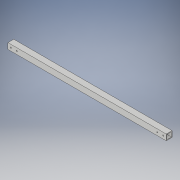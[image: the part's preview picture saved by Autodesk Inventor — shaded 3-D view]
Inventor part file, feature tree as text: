
AUTODESK INVENTOR PART (.ipt)
format: ipt  version: 2018 (Build 220112000, 112)  size: 121,856 bytes
history: native  units: in
note: dims shown in document units (in); Inventor stores cm internally (conversion verified against a paired STEP export)
features: extrude x2, sketch x2
ambient origin geometry x8: Origin, YZ Plane, XZ Plane, XY Plane, X Axis, Y Axis, Z Axis, Center Point
bodies: Solid1 (feature_tree)
feature tree (4):
  extrude  "Extrusion1"  Depth=1.0in
  extrude  "Extrusion3"  Depth=27.0in TaperAngle=0.0deg
  sketch  "Sketch1"  dims[d0=1.0in d1=1.0in]
  sketch  "Sketch3"  dims[d2=0.125in d3=27.0in d4=0.0in d7=0.5in d8=1.0in d9=0.5in d10=1.0in d11=0.2031in d12=0.2031in d13=0.2031in d14=0.2031in d15=23.0in d16=0.0in]
